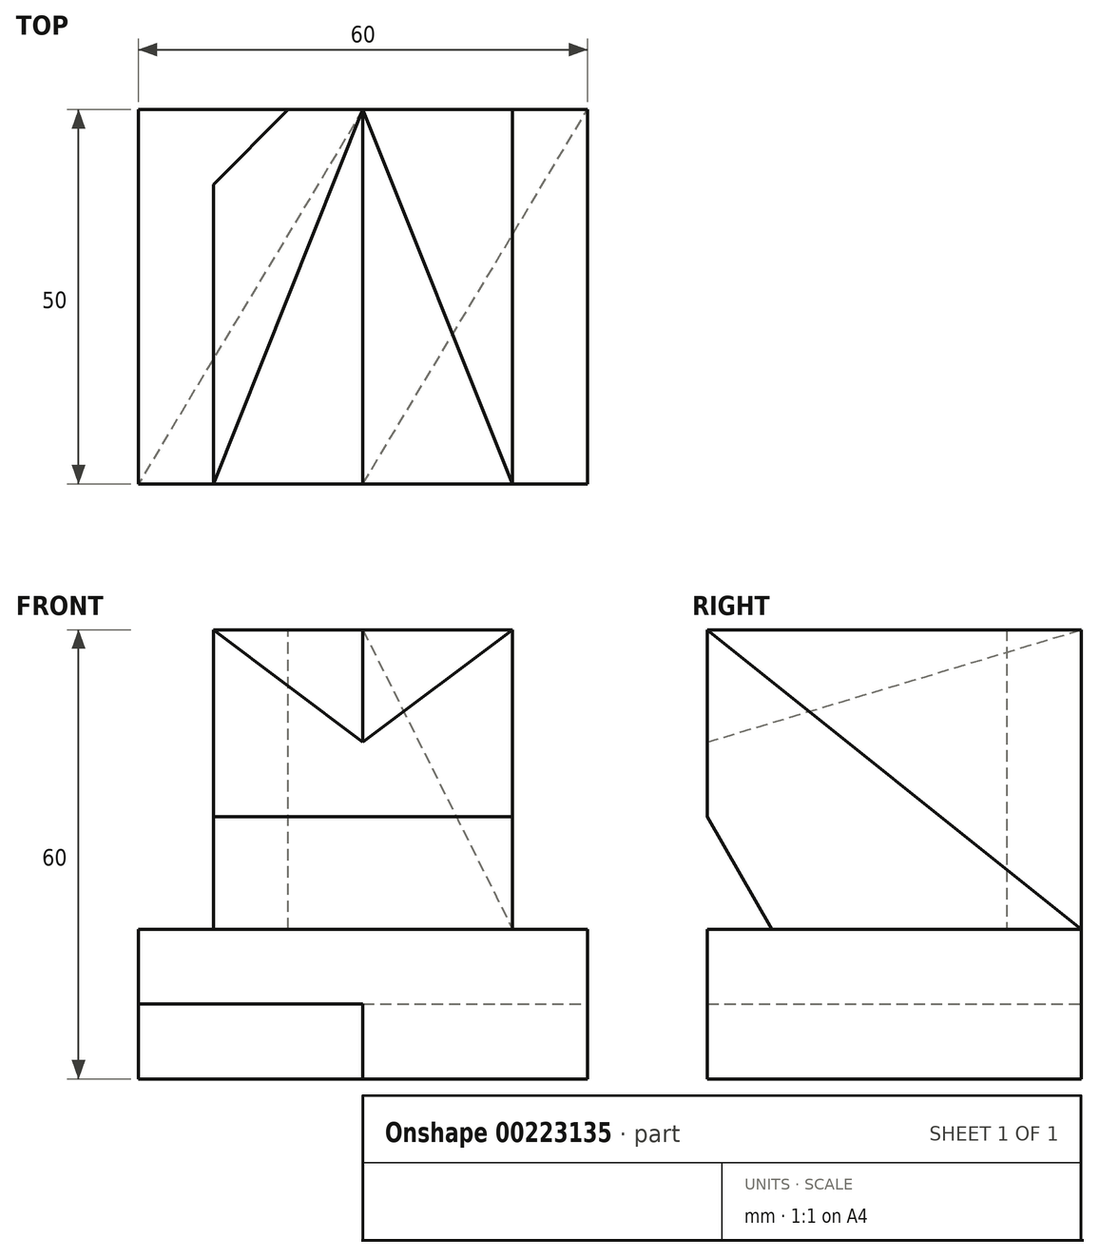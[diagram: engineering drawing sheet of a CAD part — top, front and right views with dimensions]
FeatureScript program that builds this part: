
annotation { "Feature Type Name" : "Feature", "Feature Type Description" : "" }
export const myFeature = defineFeature(function(context is Context, id is Id, definition is map)
    precondition{}
    {
        {
            var Q0;
            Q0=qCreatedBy(makeId("Top.planeOp"),FACE);
            var sketch = newSketch(context, id + "F0", { "sketchPlane" : qUnion([Q0])});
            skLineSegment(sketch, "E0.bottom", {"start": v(0, 0) * mm, "end": v(60, 0) * mm});
            skLineSegment(sketch, "E0.top", {"start": v(0, 50) * mm, "end": v(60, 50) * mm});
            skLineSegment(sketch, "E0.left", {"start": v(0, 0) * mm, "end": v(0, 50) * mm});
            skLineSegment(sketch, "E0.right", {"start": v(60, 0) * mm, "end": v(60, 50) * mm});
            skSolve(sketch);
        }
        {
            var Q0;
            Q0 = qSketchRegion(id + "F0", true);
            extrude(context, id + "F1", {"entities" : qUnion([Q0]), "depth" : 20 * mm});
        }
        {
            var Q0;
            Q0=qCreatedBy(makeId("Top.planeOp"),FACE);
            cPlane(context, id + "F2", {"entities" : qUnion([Q0]), "cplaneType" : CPlaneType.OFFSET, "offset" : 10 * mm, "width" : 150 * mm, "height" : 150 * mm});
        }
        {
            var Q0;
            Q0=makeQuery(id+"F1.opExtrude","CAP_FACE",FACE,{"disambiguationData":[OSD([sQuery(id+"F0.wireOp",EDGE,"E0.bottom"),sQuery(id+"F0.wireOp",EDGE,"E0.top"),sQuery(id+"F0.wireOp",EDGE,"E0.left"),sQuery(id+"F0.wireOp",EDGE,"E0.right")])],"isStart":true});
            var sketch = newSketch(context, id + "F3", { "sketchPlane" : qUnion([Q0])});
            skLineSegment(sketch, "E1", {"start": v(0, 0) * mm, "end": v(30, 0) * mm});
            skLineSegment(sketch, "E2", {"start": v(30, 0) * mm, "end": v(60, -50) * mm});
            skLineSegment(sketch, "E3", {"start": v(60, -50) * mm, "end": v(30, -50) * mm});
            skLineSegment(sketch, "E4", {"start": v(30, -50) * mm, "end": v(0, 0) * mm});
            skSolve(sketch);
        }
        {
            var Q0;
            Q0 = qSketchRegion(id + "F3", true);
            var Q1;
            Q1=qCreatedBy(id+"F2.planeOp",FACE);
            extrude(context, id + "F4", {"entities" : qUnion([Q0]), "operationType" : NewBodyOperationType.REMOVE, "endBound" : BoundingType.UP_TO_SURFACE, "oppositeDirection" : true, "endBoundEntityFace" : qUnion([Q1]), "depth" : 25 * mm});
        }
        {
            var Q0;
            Q0=makeQuery(id+"F1.opExtrude","CAP_FACE",FACE,{"disambiguationData":[OSD([sQuery(id+"F0.wireOp",EDGE,"E0.bottom"),sQuery(id+"F0.wireOp",EDGE,"E0.top"),sQuery(id+"F0.wireOp",EDGE,"E0.left"),sQuery(id+"F0.wireOp",EDGE,"E0.right")])],"isStart":false});
            var sketch = newSketch(context, id + "F5", { "sketchPlane" : qUnion([Q0])});
            skLineSegment(sketch, "E5.bottom", {"start": v(10, 50) * mm, "end": v(50, 50) * mm});
            skLineSegment(sketch, "E5.top", {"start": v(10, 0) * mm, "end": v(50, 0) * mm});
            skLineSegment(sketch, "E5.left", {"start": v(10, 50) * mm, "end": v(10, 0) * mm});
            skLineSegment(sketch, "E5.right", {"start": v(50, 50) * mm, "end": v(50, 0) * mm});
            skSolve(sketch);
        }
        {
            var Q0;
            Q0 = qSketchRegion(id + "F5", true);
            extrude(context, id + "F6", {"entities" : qUnion([Q0]), "operationType" : NewBodyOperationType.ADD, "depth" : 40 * mm});
        }
        {
            var Q0;
            Q0=makeQuery(id+"F6.opExtrude","SWEPT_EDGE",EDGE,{"disambiguationData":[OSD([sQuery(id+"F0.wireOp",EDGE,"E0.top"),sQuery(id+"F5.wireOp",EDGE,"E5.bottom"),sQuery(id+"F5.wireOp",EDGE,"E5.left")])]});
            chamfer(context, id + "F7", {"entities" : qUnion([Q0]), "width" : 10 * mm, "tangentPropagation" : true});
        }
        {
            var Q0;
            Q0=makeQuery(id+"F6.opExtrude","SWEPT_FACE",FACE,{"disambiguationData":[OSD([sQuery(id+"F5.wireOp",EDGE,"E5.right")])]});
            var sketch = newSketch(context, id + "F8", { "sketchPlane" : qUnion([Q0])});
            skLineSegment(sketch, "E6", {"start": v(0, 20) * mm, "end": v(0, 35) * mm});
            skLineSegment(sketch, "E7", {"start": v(0, 35) * mm, "end": v(8.66, 20) * mm});
            skLineSegment(sketch, "E8", {"start": v(8.66, 20) * mm, "end": v(0, 20) * mm});
            skSolve(sketch);
        }
        {
            var Q0;
            Q0 = qSketchRegion(id + "F8", true);
            extrude(context, id + "F9", {"entities" : qUnion([Q0]), "operationType" : NewBodyOperationType.REMOVE, "endBound" : BoundingType.UP_TO_NEXT, "oppositeDirection" : true, "depth" : 25 * mm});
        }
        {
            var Q0;
            Q0=makeQuery(id+"F6.opExtrude","SWEPT_FACE",FACE,{"disambiguationData":[OSD([sQuery(id+"F5.wireOp",EDGE,"E5.left")])]});
            cPlane(context, id + "F10", {"entities" : qUnion([Q0]), "cplaneType" : CPlaneType.OFFSET, "offset" : 20 * mm, "oppositeDirection" : true, "width" : 150 * mm, "height" : 150 * mm});
        }
        {
            var Q0;
            Q0=qCreatedBy(id+"F10.planeOp",FACE);
            var sketch = newSketch(context, id + "F11", { "sketchPlane" : qUnion([Q0])});
            skLineSegment(sketch, "E9", {"start": v(0, 45) * mm, "end": v(-50, 60) * mm});
            skSolve(sketch);
        }
        {
            var Q0;
            {var subQ1=sQuery(id+"F5.wireOp",EDGE,"E5.left");var subQ2=sQuery(id+"F5.wireOp",EDGE,"E5.top");Q0=makeQuery(id+"F9.boolean.opBoolean","SPLIT",FACE,{"disambiguationData":[TD([makeQuery(id+"F6.opExtrude","SWEPT_FACE",FACE,{"disambiguationData":[OSD([subQ1])]})])],"derivedFrom":makeQuery(id+"F6.boolean.opBoolean","MERGE",FACE,{"derivedFrom":[makeQuery(id+"F1.opExtrude","SWEPT_FACE",FACE,{"disambiguationData":[OSD([sQuery(id+"F0.wireOp",EDGE,"E0.bottom")])]}),makeQuery(id+"F6.opExtrude","SWEPT_FACE",FACE,{"disambiguationData":[OSD([subQ2])]})]})});}
            var sketch = newSketch(context, id + "F12", { "sketchPlane" : qUnion([Q0])});
            skLineSegment(sketch, "E10", {"start": v(10, 60) * mm, "end": v(50, 60) * mm});
            skLineSegment(sketch, "E11", {"start": v(50, 60) * mm, "end": v(30, 45) * mm});
            skLineSegment(sketch, "E12", {"start": v(30, 45) * mm, "end": v(10, 60) * mm});
            skSolve(sketch);
        }
        {
            var Q0;
            Q0=makeQuery(id+"F12.imprint","IMPRINT",FACE,{"disambiguationData":[TD([[makeQuery(id+"F12.imprint","IMPRINT",EDGE,{"derivedFrom":sQuery(id+"F12.wireOp",EDGE,"E10")}),-1.0]])]});
            var Q1;
            Q1=sQuery(id+"F11.wireOp",EDGE,"E9");
            sweep(context, id + "F13", {"operationType" : NewBodyOperationType.REMOVE, "profiles" : qUnion([Q0]), "path" : qUnion([Q1])});
        }
        {
            var Q0;
            {var subQ0=sQuery(id+"F5.wireOp",EDGE,"E5.right");var subQ1=sQuery(id+"F5.wireOp",EDGE,"E5.top");var subQ2=sQuery(id+"F0.wireOp",EDGE,"E0.bottom");Q0=makeQuery(id+"F13.boolean.opBoolean","MERGE",VERTEX,{"derivedFrom":[makeQuery(id+"F6.opExtrude","CAP_VERTEX",VERTEX,{"disambiguationData":[OSD([subQ2,subQ1,subQ0])],"isStart":false}),makeQuery(id+"F13.opSweep","CAP_VERTEX",VERTEX,{"disambiguationData":[OSD([subQ2,subQ1,subQ0,sQuery(id+"F11.wireOp",EDGE,"E9"),sQuery(id+"F12.wireOp",EDGE,"E10"),sQuery(id+"F12.wireOp",EDGE,"E11")])],"isStart":true})]});}
            var Q1;
            Q1=makeQuery(id+"F6.opExtrude","CAP_VERTEX",VERTEX,{"disambiguationData":[OSD([sQuery(id+"F0.wireOp",EDGE,"E0.top"),sQuery(id+"F5.wireOp",EDGE,"E5.bottom"),sQuery(id+"F5.wireOp",EDGE,"E5.right")])],"isStart":true});
            var Q2;
            Q2=makeQuery(id+"F13.boolean.opBoolean","COPY",VERTEX,{"derivedFrom":makeQuery(id+"F13.opSweep","CAP_VERTEX",VERTEX,{"disambiguationData":[OSD([sQuery(id+"F11.wireOp",EDGE,"E9"),sQuery(id+"F12.wireOp",EDGE,"E11"),sQuery(id+"F12.wireOp",EDGE,"E12")])],"isStart":false})});
            cPlane(context, id + "F14", {"entities" : qUnion([Q0, Q1, Q2]), "cplaneType" : CPlaneType.THREE_POINT, "offset" : 25 * mm, "width" : 150 * mm, "height" : 150 * mm});
        }
        {
            var Q0;
            Q0=qCreatedBy(id+"F14.planeOp",FACE);
            var sketch = newSketch(context, id + "F15", { "sketchPlane" : qUnion([Q0])});
            skLineSegment(sketch, "E13", {"start": v(24.1, 31.3) * mm, "end": v(-29, 40.25) * mm});
            skLineSegment(sketch, "E14", {"start": v(-29, 40.25) * mm, "end": v(-29, -4.47) * mm});
            skLineSegment(sketch, "E15", {"start": v(-29, -4.47) * mm, "end": v(24.1, 31.3) * mm});
            skSolve(sketch);
        }
        {
            var Q0;
            Q0 = qSketchRegion(id + "F15", true);
            extrude(context, id + "F16", {"entities" : qUnion([Q0]), "operationType" : NewBodyOperationType.REMOVE, "endBound" : BoundingType.UP_TO_NEXT, "oppositeDirection" : true, "depth" : 25 * mm});
        }
    });
